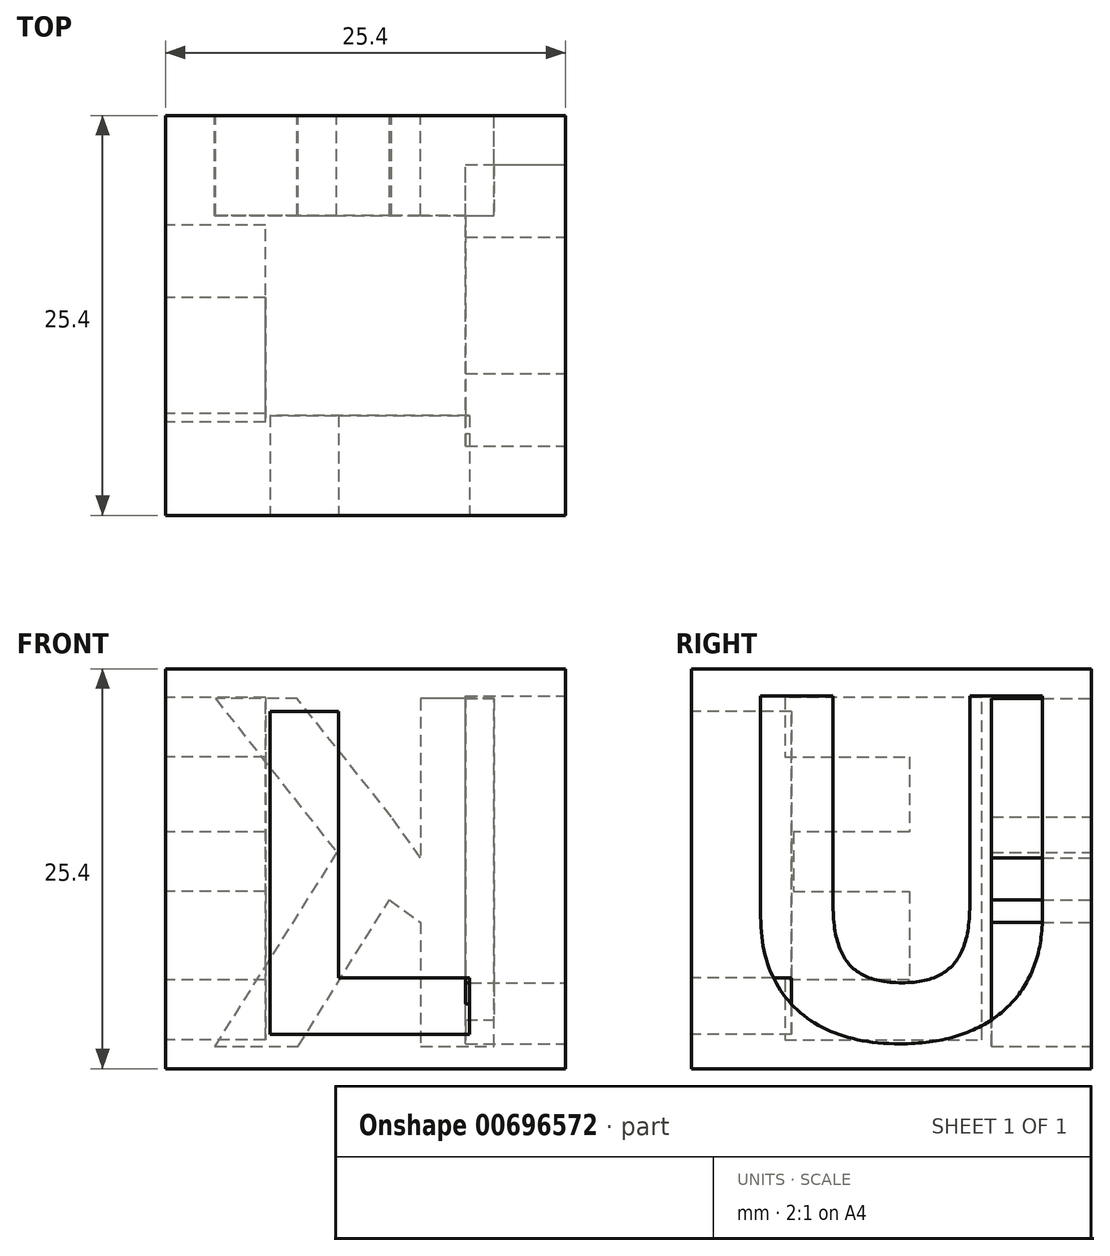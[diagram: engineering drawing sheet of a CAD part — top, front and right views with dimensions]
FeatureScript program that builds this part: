
annotation { "Feature Type Name" : "Feature", "Feature Type Description" : "" }
export const myFeature = defineFeature(function(context is Context, id is Id, definition is map)
    precondition{}
    {
        {
            var Q0;
            Q0=qCreatedBy(makeId("Front.planeOp"),FACE);
            var sketch = newSketch(context, id + "F0", { "sketchPlane" : qUnion([Q0])});
            skLineSegment(sketch, "E0.bottom", {"start": v(-12.7, 12.7) * mm, "end": v(12.7, 12.7) * mm});
            skLineSegment(sketch, "E0.top", {"start": v(-12.7, -12.7) * mm, "end": v(12.7, -12.7) * mm});
            skLineSegment(sketch, "E0.left", {"start": v(-12.7, 12.7) * mm, "end": v(-12.7, -12.7) * mm});
            skLineSegment(sketch, "E0.right", {"start": v(12.7, 12.7) * mm, "end": v(12.7, -12.7) * mm});
            skPoint(sketch, "E0.middle", {"position": v(0, 0) * mm});
            skSolve(sketch);
        }
        {
            var Q0;
            Q0 = qSketchRegion(id + "F0", true);
            extrude(context, id + "F1", {"entities" : qUnion([Q0]), "depth" : 25.4 * mm, "offsetDistance" : 25.4 * mm});
        }
        {
            var Q0;
            Q0=makeQuery(id+"F1.opExtrude","CAP_FACE",FACE,{"disambiguationData":[OSD([sQuery(id+"F0.wireOp",EDGE,"E0.bottom"),sQuery(id+"F0.wireOp",EDGE,"E0.top"),sQuery(id+"F0.wireOp",EDGE,"E0.left"),sQuery(id+"F0.wireOp",EDGE,"E0.right")])],"isStart":false});
            var sketch = newSketch(context, id + "F2", { "sketchPlane" : qUnion([Q0])});
            skText(sketch, "E1", { "text": "L", "fontName": "OpenSans-Bold.ttf"});
            const initialGuessF2  = {"E1": [-0.00863, -0.01052, 1, 0, 0.02067]};
            skSetInitialGuess(sketch, initialGuessF2);
            skSolve(sketch);
        }
        {
            var Q0;
            Q0 = qSketchRegion(id + "F2", true);
            extrude(context, id + "F3", {"entities" : qUnion([Q0]), "operationType" : NewBodyOperationType.REMOVE, "oppositeDirection" : true, "depth" : 6.35 * mm, "offsetDistance" : 25.4 * mm});
        }
        {
            var Q0;
            Q0=makeQuery(id+"F1.opExtrude","SWEPT_FACE",FACE,{"disambiguationData":[OSD([sQuery(id+"F0.wireOp",EDGE,"E0.right")])]});
            var sketch = newSketch(context, id + "F4", { "sketchPlane" : qUnion([Q0])});
            skText(sketch, "E2", { "text": "U", "fontName": "OpenSans-Bold.ttf"});
            const initialGuessF4  = {"E2": [-0.0236, -0.01082, 1, 0, 0.02198]};
            skSetInitialGuess(sketch, initialGuessF4);
            skSolve(sketch);
        }
        {
            var Q0;
            Q0 = qSketchRegion(id + "F4", true);
            extrude(context, id + "F5", {"entities" : qUnion([Q0]), "operationType" : NewBodyOperationType.REMOVE, "oppositeDirection" : true, "depth" : 6.35 * mm, "offsetDistance" : 25.4 * mm});
        }
        {
            var Q0;
            Q0=makeQuery(id+"F1.opExtrude","CAP_FACE",FACE,{"disambiguationData":[OSD([sQuery(id+"F0.wireOp",EDGE,"E0.bottom"),sQuery(id+"F0.wireOp",EDGE,"E0.top"),sQuery(id+"F0.wireOp",EDGE,"E0.left"),sQuery(id+"F0.wireOp",EDGE,"E0.right")])],"isStart":true});
            var sketch = newSketch(context, id + "F6", { "sketchPlane" : qUnion([Q0])});
            skText(sketch, "E3", { "text": "K", "fontName": "OpenSans-Bold.ttf"});
            const initialGuessF6  = {"E3": [-0.01095, -0.01128, 1, 0, 0.02227]};
            skSetInitialGuess(sketch, initialGuessF6);
            skSolve(sketch);
        }
        {
            var Q0;
            Q0 = qSketchRegion(id + "F6", true);
            extrude(context, id + "F7", {"entities" : qUnion([Q0]), "operationType" : NewBodyOperationType.REMOVE, "oppositeDirection" : true, "depth" : 6.35 * mm, "offsetDistance" : 25.4 * mm});
        }
        {
            var Q0;
            Q0=makeQuery(id+"F1.opExtrude","SWEPT_FACE",FACE,{"disambiguationData":[OSD([sQuery(id+"F0.wireOp",EDGE,"E0.left")])]});
            var sketch = newSketch(context, id + "F8", { "sketchPlane" : qUnion([Q0])});
            skText(sketch, "E4", { "text": "E", "fontName": "OpenSans-Bold.ttf"});
            const initialGuessF8  = {"E4": [0.00422, -0.01087, 1, 0, 0.02193]};
            skSetInitialGuess(sketch, initialGuessF8);
            skSolve(sketch);
        }
        {
            var Q0;
            Q0 = qSketchRegion(id + "F8", true);
            extrude(context, id + "F9", {"entities" : qUnion([Q0]), "operationType" : NewBodyOperationType.REMOVE, "oppositeDirection" : true, "depth" : 6.35 * mm, "offsetDistance" : 25.4 * mm});
        }
    });
